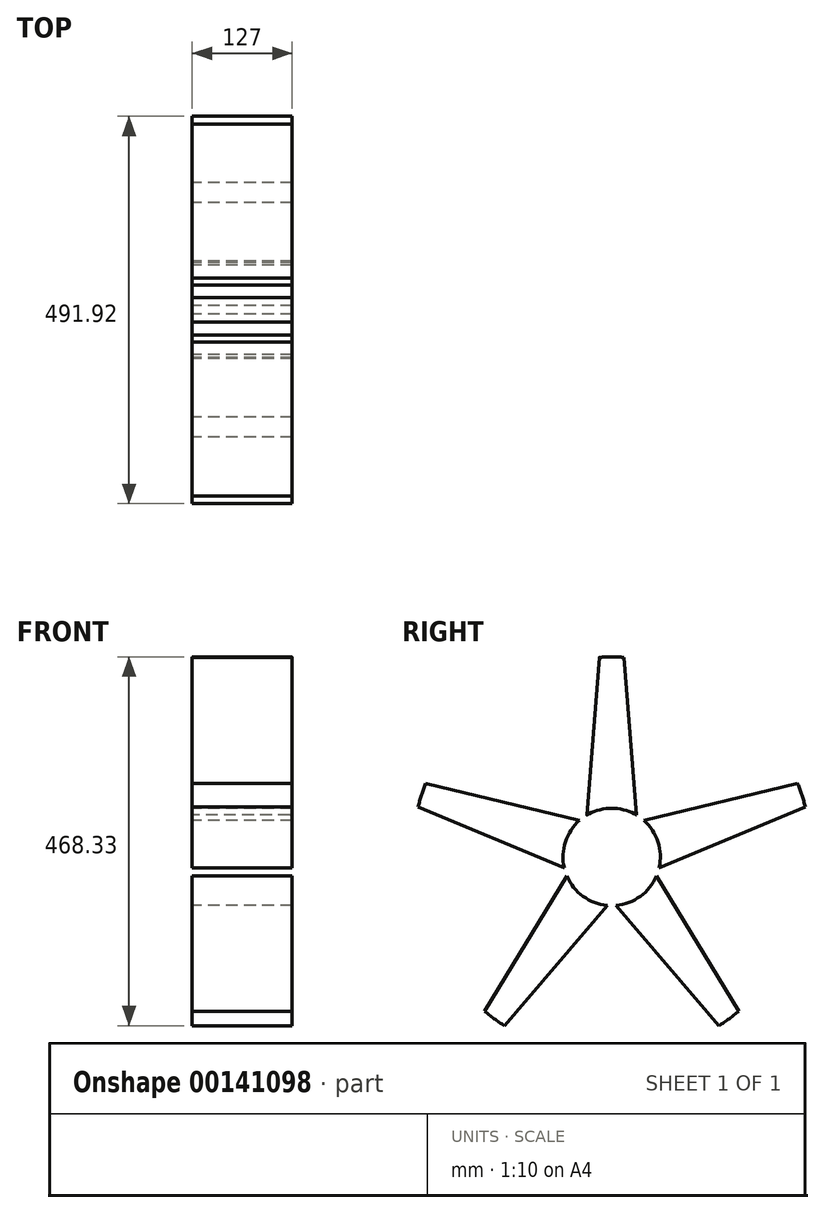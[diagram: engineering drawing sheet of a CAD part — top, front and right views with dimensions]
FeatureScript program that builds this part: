
annotation { "Feature Type Name" : "Feature", "Feature Type Description" : "" }
export const myFeature = defineFeature(function(context is Context, id is Id, definition is map)
    precondition{}
    {
        {
            var Q0;
            Q0=qCreatedBy(makeId("Right.planeOp"),FACE);
            var sketch = newSketch(context, id + "F0", { "sketchPlane" : qUnion([Q0])});
            skCircle(sketch, "E0", {"center": v(0, 0) * mm, "radius": 254 * mm});
            skCircle(sketch, "E1", {"center": v(0, 0) * mm, "radius": 61.83 * mm});
            skLineSegment(sketch, "E2", {"start": v(0, 0) * mm, "end": v(0, 279.43) * mm, "construction": true});
            skLineSegment(sketch, "E3", {"start": v(-31.67, 53.1) * mm, "end": v(-15.7, 253.51) * mm});
            skLineSegment(sketch, "E4.MirrorCS", {"start": v(31.67, 53.1) * mm, "end": v(15.7, 253.51) * mm});
            skLineSegment(sketch, "E5.1.0", {"start": v(-40.72, 46.53) * mm, "end": v(-236.25, 93.28) * mm});
            skLineSegment(sketch, "E5.1.1", {"start": v(-60.3, -13.71) * mm, "end": v(-245.96, 63.4) * mm});
            skLineSegment(sketch, "E5.2.0", {"start": v(-56.84, -24.35) * mm, "end": v(-161.72, -195.87) * mm});
            skLineSegment(sketch, "E5.2.1", {"start": v(-5.6, -61.58) * mm, "end": v(-136.3, -214.33) * mm});
            skLineSegment(sketch, "E5.3.0", {"start": v(5.6, -61.58) * mm, "end": v(136.3, -214.33) * mm});
            skLineSegment(sketch, "E5.3.1", {"start": v(56.84, -24.35) * mm, "end": v(161.72, -195.87) * mm});
            skLineSegment(sketch, "E5.4.0", {"start": v(60.3, -13.71) * mm, "end": v(245.96, 63.4) * mm});
            skLineSegment(sketch, "E5.4.1", {"start": v(40.72, 46.53) * mm, "end": v(236.25, 93.28) * mm});
            skSolve(sketch);
        }
        {
            var Q0;
            {var subQ0=sQuery(id+"F0.wireOp",EDGE,"E5.4.0");Q0=makeQuery(id+"F0.imprint","IMPRINT",FACE,{"disambiguationData":[TD([[makeQuery(id+"F0.imprint","IMPRINT",EDGE,{"derivedFrom":subQ0}),1.0]])]});}
            var Q1;
            {var subQ0=sQuery(id+"F0.wireOp",EDGE,"E3");Q1=makeQuery(id+"F0.imprint","IMPRINT",FACE,{"disambiguationData":[TD([[makeQuery(id+"F0.imprint","IMPRINT",EDGE,{"derivedFrom":subQ0}),-1.0]])]});}
            var Q2;
            {var subQ0=sQuery(id+"F0.wireOp",EDGE,"E5.1.0");Q2=makeQuery(id+"F0.imprint","IMPRINT",FACE,{"disambiguationData":[TD([[makeQuery(id+"F0.imprint","IMPRINT",EDGE,{"derivedFrom":subQ0}),1.0]])]});}
            var Q3;
            {var subQ0=sQuery(id+"F0.wireOp",EDGE,"E5.2.0");Q3=makeQuery(id+"F0.imprint","IMPRINT",FACE,{"disambiguationData":[TD([[makeQuery(id+"F0.imprint","IMPRINT",EDGE,{"derivedFrom":subQ0}),1.0]])]});}
            var Q4;
            {var subQ0=sQuery(id+"F0.wireOp",EDGE,"E5.3.0");Q4=makeQuery(id+"F0.imprint","IMPRINT",FACE,{"disambiguationData":[TD([[makeQuery(id+"F0.imprint","IMPRINT",EDGE,{"derivedFrom":subQ0}),1.0]])]});}
            extrude(context, id + "F1", {"entities" : qUnion([Q0, Q1, Q2, Q3, Q4]), "depth" : 127 * mm});
        }
        {
            var Q0;
            Q0=makeQuery(id+"F1.opExtrude","CAP_EDGE",EDGE,{"disambiguationData":[OSD([sQuery(id+"F0.wireOp",EDGE,"E4.MirrorCS")])],"isStart":false});
            var Q1;
            Q1=makeQuery(id+"F1.opExtrude","CAP_EDGE",EDGE,{"disambiguationData":[OSD([sQuery(id+"F0.wireOp",EDGE,"E3")])],"isStart":false});
            fillet(context, id + "F2", {"entities" : qUnion([Q0, Q1]), "radius" : 2.54 * mm, "tangentPropagation" : true, "allowEdgeOverflow" : false});
        }
    });
